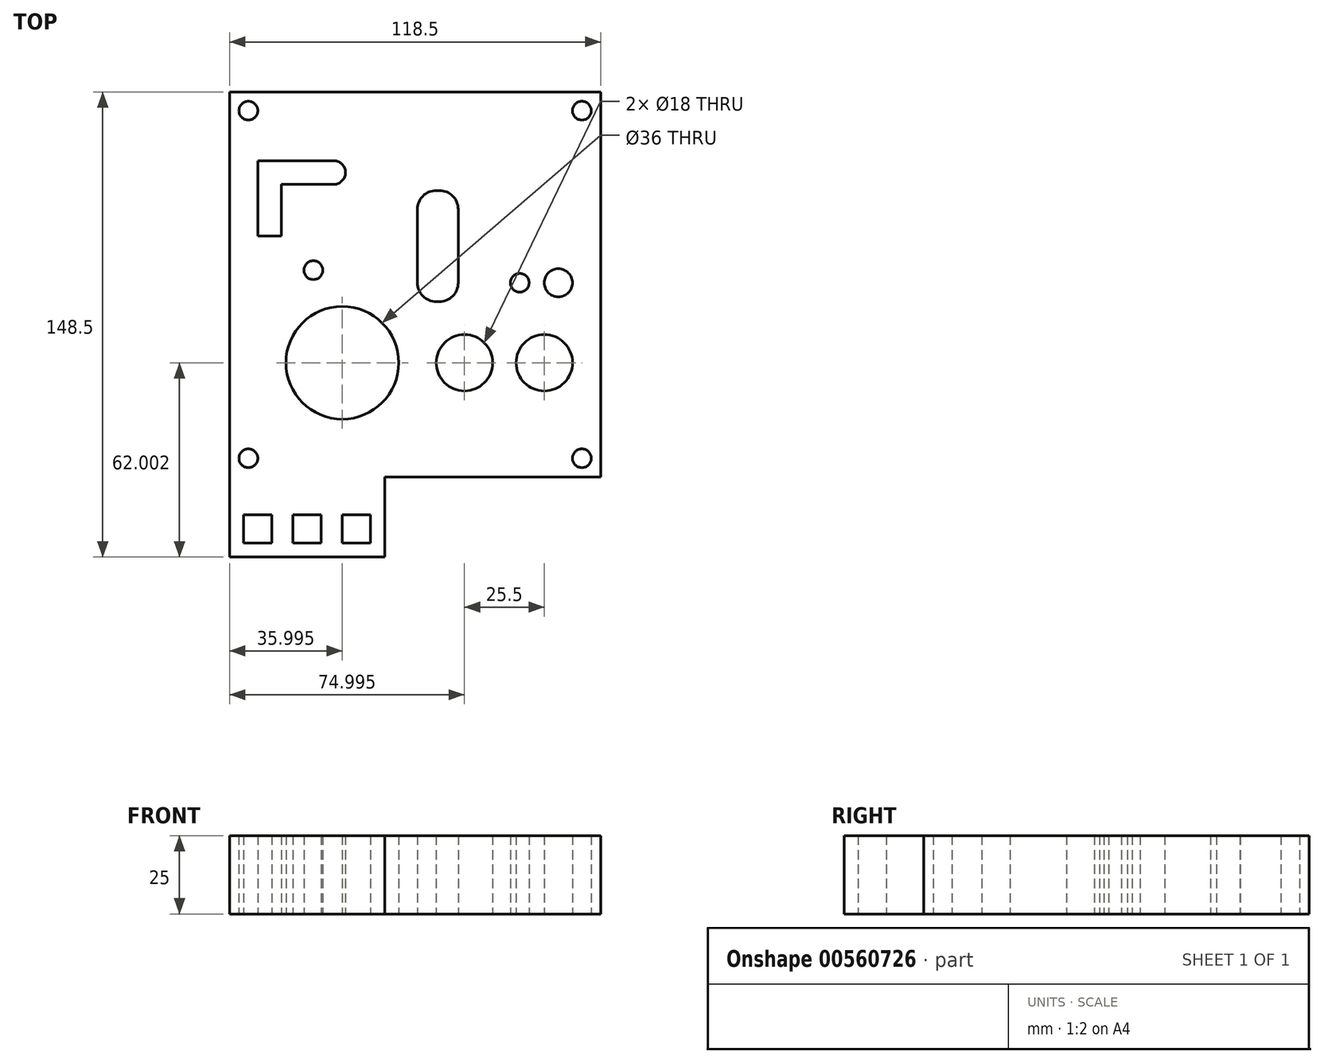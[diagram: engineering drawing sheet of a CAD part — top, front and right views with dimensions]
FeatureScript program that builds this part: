
annotation { "Feature Type Name" : "Feature", "Feature Type Description" : "" }
export const myFeature = defineFeature(function(context is Context, id is Id, definition is map)
    precondition{}
    {
        {
            var Q0;
            Q0=qCreatedBy(makeId("Top.planeOp"),FACE);
            var sketch = newSketch(context, id + "F0", { "sketchPlane" : qUnion([Q0])});
            skLineSegment(sketch, "E0", {"start": v(-58.68, 173.48) * mm, "end": v(59.82, 173.48) * mm});
            skLineSegment(sketch, "E1", {"start": v(59.82, 173.48) * mm, "end": v(59.82, 50.48) * mm});
            skLineSegment(sketch, "E2", {"start": v(-58.68, 173.48) * mm, "end": v(-58.68, 24.98) * mm});
            skCircle(sketch, "E3", {"center": v(53.82, 167.48) * mm, "radius": 3 * mm});
            skPoint(sketch, "E4.orphan", {"position": v(59.82, 167.48) * mm});
            skPoint(sketch, "E5.end.orphan", {"position": v(49.98, 167.48) * mm});
            skCircle(sketch, "E6", {"center": v(53.82, 56.48) * mm, "radius": 3 * mm});
            skPoint(sketch, "E7.orphan", {"position": v(53.82, 50.48) * mm});
            skCircle(sketch, "E8", {"center": v(-52.68, 167.48) * mm, "radius": 3 * mm});
            skPoint(sketch, "E9.start.orphan", {"position": v(-58.68, 167.48) * mm});
            skCircle(sketch, "E10", {"center": v(-52.68, 56.48) * mm, "radius": 3 * mm});
            skLineSegment(sketch, "E11", {"start": v(-49.68, 151.44) * mm, "end": v(-49.62, 127.44) * mm});
            skLineSegment(sketch, "E12", {"start": v(-49.62, 127.44) * mm, "end": v(-42.12, 127.46) * mm});
            skPoint(sketch, "E13.orphan", {"position": v(-58.68, 56.48) * mm});
            skLineSegment(sketch, "E14", {"start": v(59.82, 173.48) * mm, "end": v(59.82, 86.98) * mm});
            skPoint(sketch, "E15.end.orphan", {"position": v(41.82, 24.98) * mm});
            skPoint(sketch, "E16.end.orphan", {"position": v(16.32, 24.98) * mm});
            skPoint(sketch, "E17.end.orphan", {"position": v(-22.68, 24.98) * mm});
            skLineSegment(sketch, "E18", {"start": v(-9.18, 24.98) * mm, "end": v(-58.68, 24.98) * mm});
            skPoint(sketch, "E19.start.orphan", {"position": v(-4.68, 86.98) * mm});
            skLineSegment(sketch, "E20", {"start": v(59.82, 50.48) * mm, "end": v(-9.18, 50.48) * mm});
            skLineSegment(sketch, "E21", {"start": v(-9.18, 50.48) * mm, "end": v(-9.18, 24.98) * mm});
            skPoint(sketch, "E22.start.orphan", {"position": v(-68.15, 56.48) * mm});
            skLineSegment(sketch, "E23", {"start": v(-54.18, 38.48) * mm, "end": v(-54.18, 29.48) * mm});
            skLineSegment(sketch, "E24", {"start": v(-54.18, 29.48) * mm, "end": v(-45.18, 29.48) * mm});
            skLineSegment(sketch, "E25", {"start": v(-45.18, 29.48) * mm, "end": v(-45.18, 38.48) * mm});
            skLineSegment(sketch, "E26", {"start": v(-45.18, 38.48) * mm, "end": v(-54.18, 38.48) * mm});
            skLineSegment(sketch, "E27", {"start": v(-22.68, 38.48) * mm, "end": v(-22.68, 29.48) * mm});
            skLineSegment(sketch, "E28", {"start": v(-22.68, 29.48) * mm, "end": v(-13.68, 29.48) * mm});
            skLineSegment(sketch, "E29", {"start": v(-13.68, 29.48) * mm, "end": v(-13.68, 38.48) * mm});
            skLineSegment(sketch, "E30", {"start": v(-13.68, 38.48) * mm, "end": v(-22.68, 38.48) * mm});
            skPoint(sketch, "E31.endSnap0", {"position": v(-9.18, 37.73) * mm});
            skPoint(sketch, "E32.start.orphan", {"position": v(-40.68, 38.48) * mm});
            skPoint(sketch, "E33.end.orphan", {"position": v(-31.68, 38.48) * mm});
            skPoint(sketch, "E34.end.orphan", {"position": v(-31.68, 29.48) * mm});
            skPoint(sketch, "E34.start.orphan", {"position": v(-40.68, 29.48) * mm});
            skLineSegment(sketch, "E35", {"start": v(-38.43, 38.48) * mm, "end": v(-29.43, 38.48) * mm});
            skLineSegment(sketch, "E36", {"start": v(-29.43, 29.48) * mm, "end": v(-29.43, 38.48) * mm});
            skLineSegment(sketch, "E37", {"start": v(-29.43, 29.48) * mm, "end": v(-38.43, 29.48) * mm});
            skLineSegment(sketch, "E38", {"start": v(-38.43, 29.48) * mm, "end": v(-38.43, 38.48) * mm});
            skPoint(sketch, "E31.end.orphan", {"position": v(-9.18, 38.48) * mm});
            skPoint(sketch, "E39.center.orphan", {"position": v(-22.68, 86.98) * mm});
            skPoint(sketch, "E40.center.orphan", {"position": v(16.32, 86.98) * mm});
            skPoint(sketch, "E41.center.orphan", {"position": v(41.82, 86.98) * mm});
            skCircle(sketch, "E42", {"center": v(-22.68, 86.98) * mm, "radius": 18 * mm});
            skLineSegment(sketch, "E43", {"start": v(-22.68, 38.48) * mm, "end": v(-13.68, 38.48) * mm});
            skCircle(sketch, "E44", {"center": v(16.32, 86.98) * mm, "radius": 9 * mm});
            skCircle(sketch, "E45", {"center": v(41.82, 86.98) * mm, "radius": 9 * mm});
            skPoint(sketch, "E46.end.orphan", {"position": v(41.82, 38.48) * mm});
            skPoint(sketch, "E46.start.orphan", {"position": v(16.32, 38.48) * mm});
            skLineSegment(sketch, "E47", {"start": v(-52.68, 170.48) * mm, "end": v(-52.68, 173.48) * mm});
            skLineSegment(sketch, "E48", {"start": v(-58.68, 173.48) * mm, "end": v(7.32, 173.48) * mm});
            skLineSegment(sketch, "E49", {"start": v(1.32, 133.98) * mm, "end": v(1.32, 114.52) * mm});
            skLineSegment(sketch, "E50", {"start": v(14.32, 132.98) * mm, "end": v(14.32, 112.52) * mm});
            skLineSegment(sketch, "E51", {"start": v(1.32, 133.98) * mm, "end": v(1.32, 135.98) * mm});
            skLineSegment(sketch, "E52", {"start": v(1.32, 114.52) * mm, "end": v(1.32, 112.52) * mm});
            skLineSegment(sketch, "E53", {"start": v(14.32, 132.98) * mm, "end": v(14.32, 135.98) * mm});
            skLineSegment(sketch, "E54", {"start": v(14.32, 135.98) * mm, "end": v(14.32, 112.52) * mm});
            skLineSegment(sketch, "E55", {"start": v(14.32, 112.52) * mm, "end": v(14.32, 112.52) * mm});
            skLineSegment(sketch, "E56", {"start": v(8.32, 106.52) * mm, "end": v(7.32, 106.52) * mm});
            skLineSegment(sketch, "E57", {"start": v(7.32, 141.98) * mm, "end": v(8.32, 141.98) * mm});
            skPoint(sketch, "E58.visualSharp", {"position": v(1.32, 106.52) * mm});
            skArc(sketch, "E58.filletArc", {"start": v(1.32, 112.52) * mm, "mid": v(3.07, 108.28) * mm, "end": v(7.32, 106.52) * mm});
            skPoint(sketch, "E59.visualSharp", {"position": v(14.32, 106.52) * mm});
            skArc(sketch, "E59.filletArc", {"start": v(8.32, 106.52) * mm, "mid": v(12.56, 108.28) * mm, "end": v(14.32, 112.52) * mm});
            skPoint(sketch, "E60.visualSharp", {"position": v(1.32, 141.98) * mm});
            skArc(sketch, "E60.filletArc", {"start": v(7.32, 141.98) * mm, "mid": v(3.07, 140.23) * mm, "end": v(1.32, 135.98) * mm});
            skPoint(sketch, "E61.visualSharp", {"position": v(14.32, 141.98) * mm});
            skArc(sketch, "E61.filletArc", {"start": v(14.32, 135.98) * mm, "mid": v(12.56, 140.23) * mm, "end": v(8.32, 141.98) * mm});
            skLineSegment(sketch, "E62", {"start": v(-49.68, 151.44) * mm, "end": v(-25.68, 151.5) * mm});
            skLineSegment(sketch, "E63", {"start": v(-42.12, 127.46) * mm, "end": v(-42.1, 143.96) * mm});
            skLineSegment(sketch, "E64", {"start": v(-25.68, 143.96) * mm, "end": v(-42.1, 143.96) * mm});
            skPoint(sketch, "E65.start.orphan", {"position": v(-42.12, 151.46) * mm});
            skLineSegment(sketch, "E66", {"start": v(-25.68, 143.96) * mm, "end": v(-25.43, 143.96) * mm});
            skLineSegment(sketch, "E67", {"start": v(-21.68, 147.71) * mm, "end": v(-21.68, 147.76) * mm});
            skLineSegment(sketch, "E68", {"start": v(-25.43, 151.5) * mm, "end": v(-25.68, 151.5) * mm});
            skPoint(sketch, "E69.visualSharp", {"position": v(-21.68, 151.5) * mm});
            skArc(sketch, "E69.filletArc", {"start": v(-21.68, 147.76) * mm, "mid": v(-22.78, 150.4) * mm, "end": v(-25.43, 151.5) * mm});
            skPoint(sketch, "E70.visualSharp", {"position": v(-21.68, 143.96) * mm});
            skArc(sketch, "E70.filletArc", {"start": v(-25.43, 143.96) * mm, "mid": v(-22.78, 145.06) * mm, "end": v(-21.68, 147.71) * mm});
            skCircle(sketch, "E71", {"center": v(-31.92, 116.55) * mm, "radius": 3 * mm});
            skCircle(sketch, "E72", {"center": v(33.96, 112.52) * mm, "radius": 3 * mm});
            skCircle(sketch, "E73", {"center": v(46.3, 112.52) * mm, "radius": 4.5 * mm});
            skSolve(sketch);
        }
        {
            var Q0;
            Q0 = qSketchRegion(id + "F0", true);
            extrude(context, id + "F1", {"entities" : qUnion([Q0]), "depth" : 25 * mm, "offsetDistance" : 25 * mm});
        }
    });
